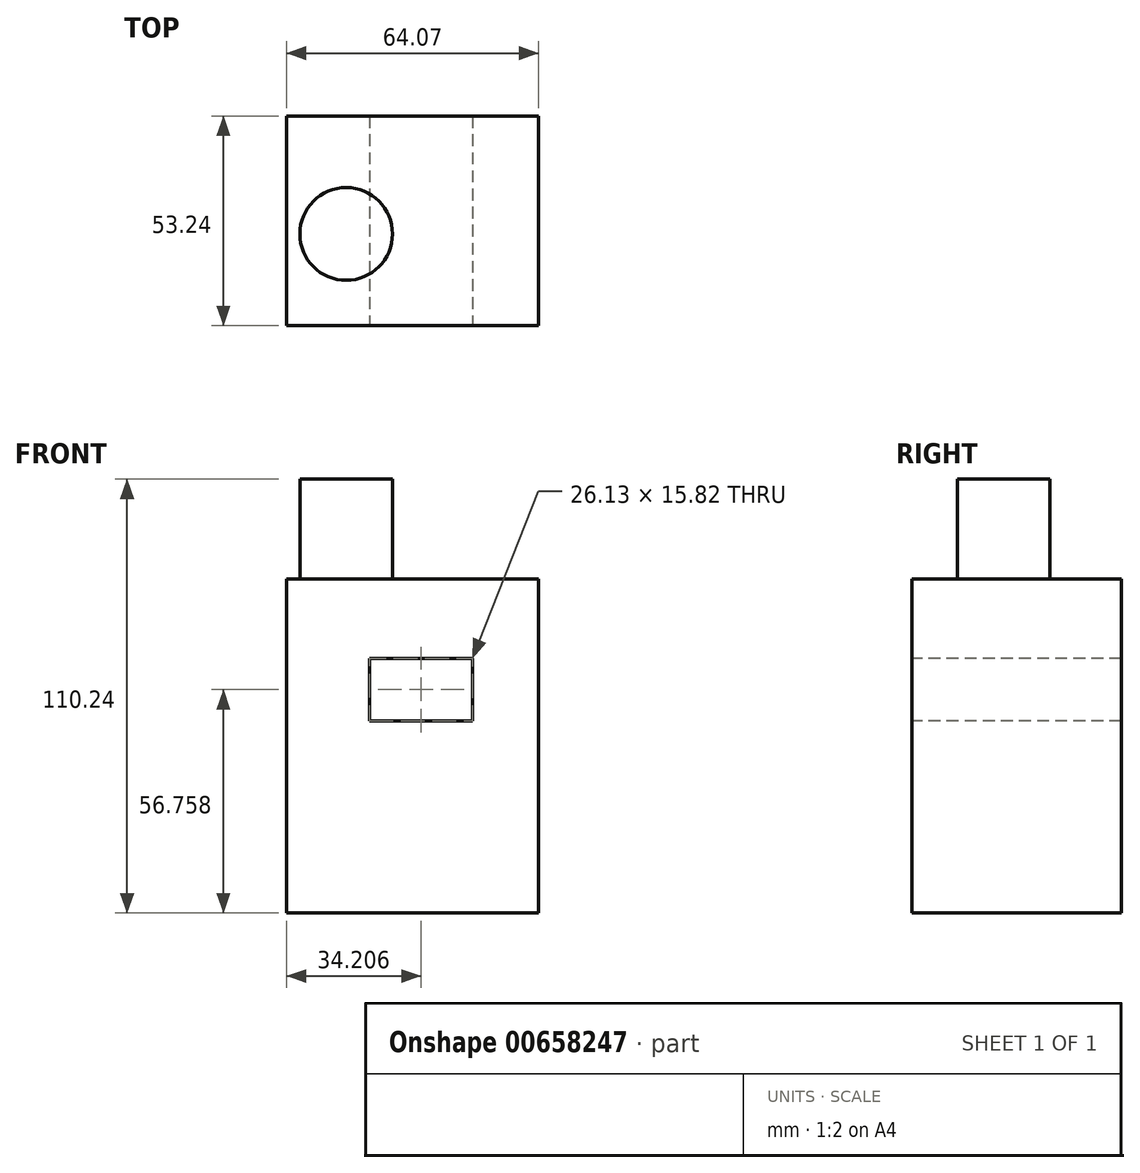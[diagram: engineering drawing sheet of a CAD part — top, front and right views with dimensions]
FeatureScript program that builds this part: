
annotation { "Feature Type Name" : "Feature", "Feature Type Description" : "" }
export const myFeature = defineFeature(function(context is Context, id is Id, definition is map)
    precondition{}
    {
        {
            var Q0;
            Q0=qCreatedBy(makeId("Top.planeOp"),FACE);
            var sketch = newSketch(context, id + "F0", { "sketchPlane" : qUnion([Q0])});
            skLineSegment(sketch, "E0.bottom", {"start": v(26.92, -23.31) * mm, "end": v(-37.15, -23.31) * mm});
            skLineSegment(sketch, "E0.top", {"start": v(26.92, 29.93) * mm, "end": v(-37.15, 29.93) * mm});
            skLineSegment(sketch, "E0.left", {"start": v(26.92, -23.31) * mm, "end": v(26.92, 29.93) * mm});
            skLineSegment(sketch, "E0.right", {"start": v(-37.15, -23.31) * mm, "end": v(-37.15, 29.93) * mm});
            skSolve(sketch);
        }
        {
            var Q0;
            Q0=makeQuery(id+"F0.imprint","IMPRINT",FACE,{"disambiguationData":[TD([[makeQuery(id+"F0.imprint","IMPRINT",EDGE,{"derivedFrom":sQuery(id+"F0.wireOp",EDGE,"E0.bottom")}),-1.0]])]});
            extrude(context, id + "F1", {"entities" : qUnion([Q0]), "depth" : 84.84 * mm, "offsetDistance" : 25.4 * mm});
        }
        {
            var Q0;
            Q0=makeQuery(id+"F1.opExtrude","CAP_FACE",FACE,{"disambiguationData":[OSD([sQuery(id+"F0.wireOp",EDGE,"E0.bottom"),sQuery(id+"F0.wireOp",EDGE,"E0.top"),sQuery(id+"F0.wireOp",EDGE,"E0.left"),sQuery(id+"F0.wireOp",EDGE,"E0.right")])],"isStart":false});
            var sketch = newSketch(context, id + "F2", { "sketchPlane" : qUnion([Q0])});
            skCircle(sketch, "E1", {"center": v(-21.95, 0) * mm, "radius": 11.77 * mm});
            skSolve(sketch);
        }
        {
            var Q0;
            Q0=makeQuery(id+"F2.imprint","IMPRINT",FACE,{"disambiguationData":[TD([[makeQuery(id+"F2.imprint","IMPRINT",EDGE,{"derivedFrom":sQuery(id+"F2.wireOp",EDGE,"E1")}),1.0]])]});
            extrude(context, id + "F3", {"entities" : qUnion([Q0]), "operationType" : NewBodyOperationType.ADD, "depth" : 25.4 * mm, "offsetDistance" : 25.4 * mm});
        }
        {
            var Q0;
            Q0=makeQuery(id+"F1.opExtrude","SWEPT_FACE",FACE,{"disambiguationData":[OSD([sQuery(id+"F0.wireOp",EDGE,"E0.bottom")])]});
            var sketch = newSketch(context, id + "F4", { "sketchPlane" : qUnion([Q0])});
            skLineSegment(sketch, "E2.bottom", {"start": v(-24.84, 35.6) * mm, "end": v(17.48, 35.6) * mm});
            skLineSegment(sketch, "E2.top", {"start": v(-24.84, 20.51) * mm, "end": v(17.48, 20.51) * mm});
            skLineSegment(sketch, "E2.left", {"start": v(-24.84, 35.6) * mm, "end": v(-24.84, 20.51) * mm});
            skLineSegment(sketch, "E2.right", {"start": v(17.48, 35.6) * mm, "end": v(17.48, 20.51) * mm});
            skLineSegment(sketch, "E3.bottom", {"start": v(-16, 64.67) * mm, "end": v(10.12, 64.67) * mm});
            skLineSegment(sketch, "E3.top", {"start": v(-16, 48.85) * mm, "end": v(10.12, 48.85) * mm});
            skLineSegment(sketch, "E3.left", {"start": v(-16, 64.67) * mm, "end": v(-16, 48.85) * mm});
            skLineSegment(sketch, "E3.right", {"start": v(10.12, 64.67) * mm, "end": v(10.12, 48.85) * mm});
            skSolve(sketch);
        }
        {
            var Q0;
            Q0=makeQuery(id+"F4.imprint","IMPRINT",FACE,{"disambiguationData":[TD([[makeQuery(id+"F4.imprint","IMPRINT",EDGE,{"derivedFrom":sQuery(id+"F4.wireOp",EDGE,"E3.bottom")}),-1.0]])]});
            extrude(context, id + "F5", {"entities" : qUnion([Q0]), "operationType" : NewBodyOperationType.REMOVE, "oppositeDirection" : true, "depth" : 82.55 * mm, "offsetDistance" : 25.4 * mm});
        }
    });
